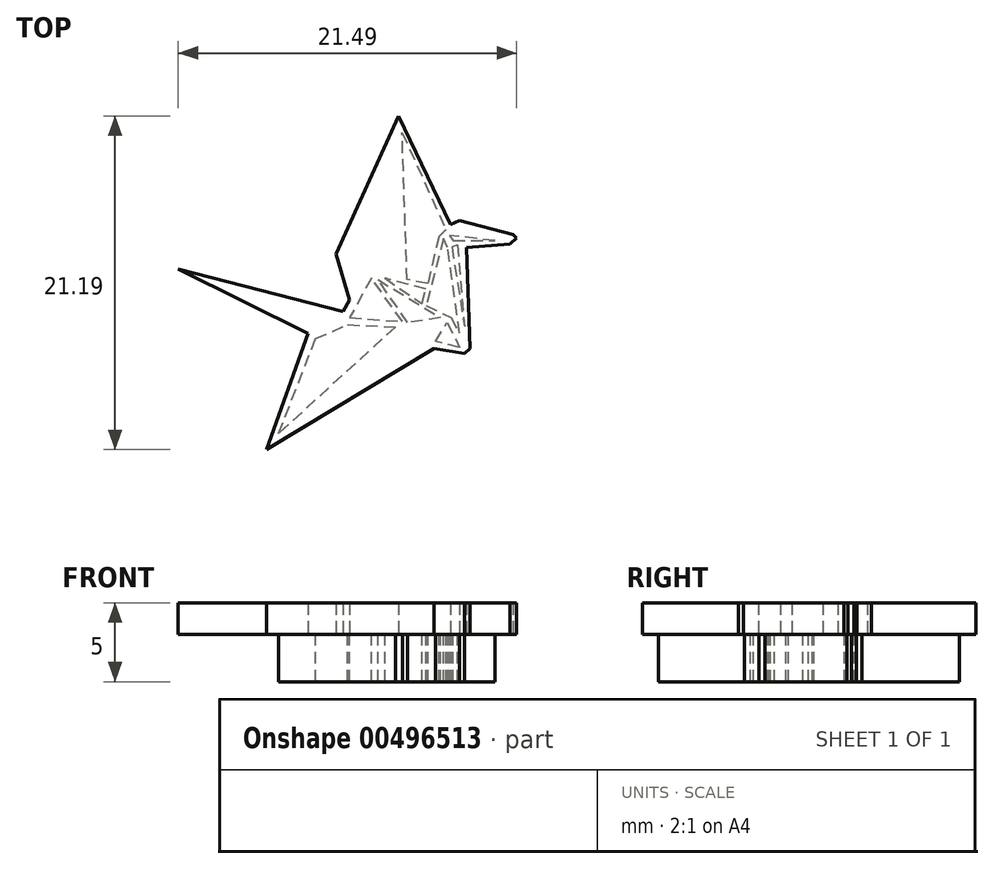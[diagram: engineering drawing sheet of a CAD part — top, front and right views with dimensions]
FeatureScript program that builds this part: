
annotation { "Feature Type Name" : "Feature", "Feature Type Description" : "" }
export const myFeature = defineFeature(function(context is Context, id is Id, definition is map)
    precondition{}
    {
        {
            var Q0;
            Q0=qCreatedBy(makeId("Top.planeOp"),FACE);
            var sketch = newSketch(context, id + "F0", { "sketchPlane" : qUnion([Q0])});
            skLineSegment(sketch, "E0", {"start": v(5.2, 14) * mm, "end": v(15.7, 11.3) * mm});
            skLineSegment(sketch, "E1", {"start": v(15.7, 11.3) * mm, "end": v(16.1, 12.01) * mm});
            skLineSegment(sketch, "E2", {"start": v(16.1, 12.01) * mm, "end": v(15.25, 14.95) * mm});
            skLineSegment(sketch, "E3", {"start": v(15.25, 14.95) * mm, "end": v(19.21, 23.72) * mm});
            skLineSegment(sketch, "E4", {"start": v(19.21, 23.72) * mm, "end": v(22.5, 16.81) * mm});
            skLineSegment(sketch, "E5", {"start": v(22.5, 16.81) * mm, "end": v(23.07, 17.08) * mm});
            skLineSegment(sketch, "E6", {"start": v(23.07, 17.08) * mm, "end": v(26.5, 16.17) * mm});
            skLineSegment(sketch, "E7", {"start": v(26.5, 16.17) * mm, "end": v(26.7, 15.95) * mm});
            skLineSegment(sketch, "E8", {"start": v(26.7, 15.95) * mm, "end": v(26.3, 15.57) * mm});
            skLineSegment(sketch, "E9", {"start": v(26.3, 15.57) * mm, "end": v(23.53, 15.34) * mm});
            skLineSegment(sketch, "E10", {"start": v(23.53, 15.34) * mm, "end": v(23.75, 8.93) * mm});
            skLineSegment(sketch, "E11", {"start": v(23.75, 8.93) * mm, "end": v(23.4, 8.62) * mm});
            skLineSegment(sketch, "E12", {"start": v(23.4, 8.62) * mm, "end": v(21.47, 8.94) * mm});
            skLineSegment(sketch, "E13", {"start": v(21.47, 8.94) * mm, "end": v(10.81, 2.53) * mm});
            skLineSegment(sketch, "E14", {"start": v(10.81, 2.53) * mm, "end": v(13.47, 9.9) * mm});
            skLineSegment(sketch, "E15", {"start": v(13.47, 9.9) * mm, "end": v(5.2, 14) * mm});
            skSolve(sketch);
        }
        {
            var Q0;
            Q0=makeQuery(id+"F0.imprint","IMPRINT",FACE,{"disambiguationData":[TD([[makeQuery(id+"F0.imprint","IMPRINT",EDGE,{"derivedFrom":sQuery(id+"F0.wireOp",EDGE,"E0")}),-1.0]])]});
            var sketch = newSketch(context, id + "F1", { "sketchPlane" : qUnion([Q0])});
            skLineSegment(sketch, "E16", {"start": v(11.6, 3.54) * mm, "end": v(13.95, 9.56) * mm});
            skLineSegment(sketch, "E17", {"start": v(13.95, 9.56) * mm, "end": v(15.98, 10.45) * mm});
            skLineSegment(sketch, "E18", {"start": v(15.98, 10.45) * mm, "end": v(19.01, 10.31) * mm});
            skLineSegment(sketch, "E19", {"start": v(19.01, 10.31) * mm, "end": v(11.6, 3.54) * mm});
            skLineSegment(sketch, "E20", {"start": v(16.1, 10.91) * mm, "end": v(19.46, 10.65) * mm});
            skLineSegment(sketch, "E21", {"start": v(19.46, 10.65) * mm, "end": v(17.48, 13.4) * mm});
            skLineSegment(sketch, "E22", {"start": v(17.48, 13.4) * mm, "end": v(16.1, 10.91) * mm});
            skLineSegment(sketch, "E23", {"start": v(17.91, 13.31) * mm, "end": v(21.87, 10.91) * mm});
            skLineSegment(sketch, "E24", {"start": v(21.87, 10.91) * mm, "end": v(19.79, 10.58) * mm});
            skLineSegment(sketch, "E25", {"start": v(19.79, 10.58) * mm, "end": v(17.91, 13.31) * mm});
            skLineSegment(sketch, "E26", {"start": v(23.08, 9.02) * mm, "end": v(21.56, 9.37) * mm});
            skLineSegment(sketch, "E27", {"start": v(20.96, 12.73) * mm, "end": v(18.34, 13.4) * mm});
            skLineSegment(sketch, "E28", {"start": v(18.34, 13.4) * mm, "end": v(20.69, 11.8) * mm});
            skLineSegment(sketch, "E29", {"start": v(20.69, 11.8) * mm, "end": v(20.96, 12.73) * mm});
            skLineSegment(sketch, "E30", {"start": v(23.08, 9.92) * mm, "end": v(22.32, 15.36) * mm});
            skLineSegment(sketch, "E31", {"start": v(22.32, 15.36) * mm, "end": v(22.06, 15.94) * mm});
            skLineSegment(sketch, "E32", {"start": v(22.06, 15.94) * mm, "end": v(20.96, 11.66) * mm});
            skLineSegment(sketch, "E33", {"start": v(20.96, 11.66) * mm, "end": v(22.55, 10.91) * mm});
            skLineSegment(sketch, "E34", {"start": v(22.55, 10.91) * mm, "end": v(23.08, 9.92) * mm});
            skLineSegment(sketch, "E35", {"start": v(21.07, 13.07) * mm, "end": v(19.75, 13.31) * mm});
            skLineSegment(sketch, "E36", {"start": v(19.75, 13.31) * mm, "end": v(19.43, 22.67) * mm});
            skLineSegment(sketch, "E37", {"start": v(19.43, 22.67) * mm, "end": v(22.23, 16.48) * mm});
            skLineSegment(sketch, "E38", {"start": v(22.23, 16.48) * mm, "end": v(21.77, 16.07) * mm});
            skLineSegment(sketch, "E39", {"start": v(21.77, 16.07) * mm, "end": v(21.07, 13.07) * mm});
            skLineSegment(sketch, "E40", {"start": v(22.96, 15.52) * mm, "end": v(22.6, 15.4) * mm});
            skLineSegment(sketch, "E41", {"start": v(22.6, 15.4) * mm, "end": v(23.4, 10.32) * mm});
            skLineSegment(sketch, "E42", {"start": v(22.96, 15.52) * mm, "end": v(23.4, 10.32) * mm});
            skLineSegment(sketch, "E43", {"start": v(22.45, 16.12) * mm, "end": v(22.67, 15.79) * mm});
            skLineSegment(sketch, "E44", {"start": v(22.67, 15.79) * mm, "end": v(25.33, 15.79) * mm});
            skLineSegment(sketch, "E45", {"start": v(25.33, 15.79) * mm, "end": v(22.45, 16.12) * mm});
            skLineSegment(sketch, "E46", {"start": v(21.56, 9.37) * mm, "end": v(22.3, 10.6) * mm});
            skLineSegment(sketch, "E47", {"start": v(22.3, 10.6) * mm, "end": v(23.08, 9.02) * mm});
            skSolve(sketch);
        }
        {
            var Q0;
            Q0 = qSketchRegion(id + "F0", true);
            extrude(context, id + "F2", {"entities" : qUnion([Q0]), "depth" : 2 * mm, "offsetDistance" : 25 * mm});
        }
        {
            var Q0;
            Q0 = qSketchRegion(id + "F1", true);
            extrude(context, id + "F3", {"entities" : qUnion([Q0]), "depth" : -3 * mm, "offsetDistance" : 25 * mm});
        }
    });
